# Revit family: Bernhardt_Design-Tables-Freestanding-Frame_36h-Blueprint
name_source: partatom
category: Furniture
revit_build: Autodesk Revit 2016 (Build: 20150714_1515(x64)
units: mm (PartAtom-declared; Revit-internal decimal feet)

## family parameters
Always vertical = Yes
Cut with Voids When Loaded = No
OmniClass Number = 23.40.20.00
OmniClass Title = General Furniture and Specialties
Room Calculation Point = No
Shared = No
Work Plane-Based = No

## types (9) — shared parameters
BlackPaint = Black Paint
Blueprint Gray = Blueprint Gray
LegDistance = 20"
LegHeight = 35"
Manufacturer = Bernhardt Design
Model = Blueprint
RailCap = 0"
RailCapFront = 2"
TableTop = <By Category>
TableTopHeight = 35"
TotalHeight = 36"
URL = http://www.bernhardtdesign.com
Wood = <By Category>

## per-type parameters (varying)
| type | CapDistance | Railing_bottom | Railing_top | Spacer_120in | Spacer_72in | Spacer_96in | TableDepth | TableWidth | TotalDepth | TotalWidth |
| BPS-BGC-AARR000 | 26 1/2" | -24 1/2" | 24 1/2" | No | Yes | No | 24" | 36" | 48" | 72" |
| BPS-BGA-AARR000 | 26 1/2" | -24 1/2" | 24 1/2" | No | Yes | No | 18" | 36" | 36" | 72" |
| BPS-BKC-AARR000 | 38 1/2" | -36 1/2" | 36 1/2" | No | No | Yes | 24" | 48" | 48" | 96" |
| BPS-BOC-AARR000 | 38 1/2" | -36 1/2" | 36 1/2" | Yes | Yes | No | 24" | 60" | 48" | 120" |
| BPS-BKA-AARR000 | 38 1/2" | -36 1/2" | 36 1/2" | No | No | Yes | 18" | 48" | 36" | 96" |
| BPS-BGB-AARR000 | 26 1/2" | -24 1/2" | 24 1/2" | No | Yes | No | 21" | 36" | 42" | 72" |
| BPS-BKB-AARR000 | 38 1/2" | -36 1/2" | 36 1/2" | No | No | Yes | 21" | 48" | 42" | 96" |
| BPS-BOA-AARR000 | 38 1/2" | -36 1/2" | 36 1/2" | Yes | Yes | No | 18" | 60" | 36" | 120" |
| BPS-BOB-AARR000 | 38 1/2" | -36 1/2" | 36 1/2" | Yes | Yes | No | 21" | 60" | 42" | 120" |

note: column(s) folded — value = type name in every type: Catalog, SKU

## geometry (parser evidence)
native form markers: Sweep x1
no freeform markers — native parametric forms only
